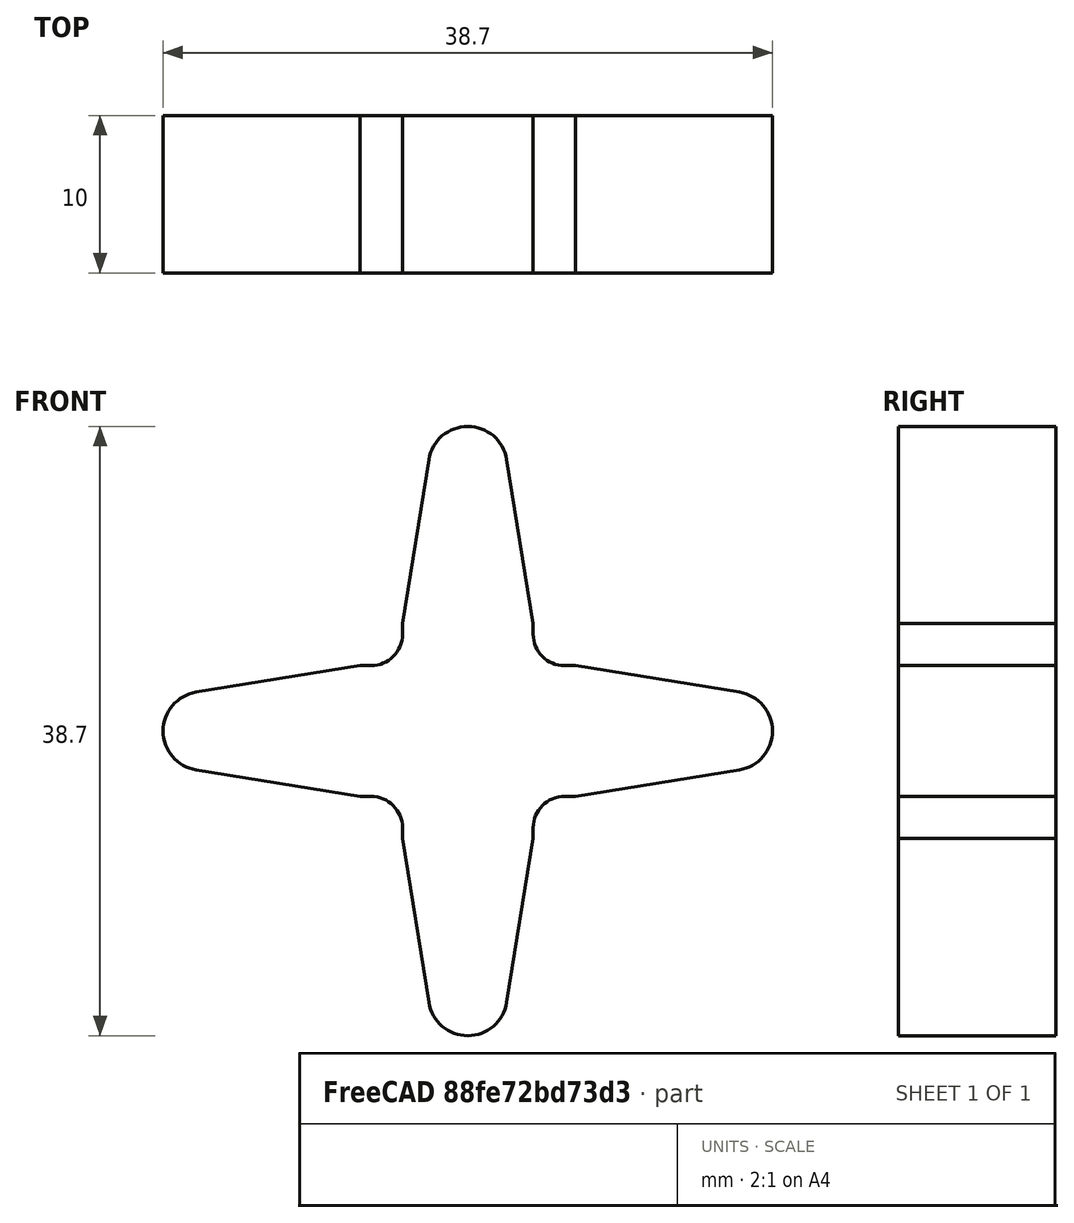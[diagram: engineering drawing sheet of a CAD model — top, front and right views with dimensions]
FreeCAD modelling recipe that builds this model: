
FCSTD DOCUMENT  (FreeCAD 0.16R6707 (Git))
Label: Corona_Futaba_3003
License: CreativeCommons Attribution-ShareAlike
LicenseURL: http://creativecommons.org/licenses/by-sa/4.0/
objects: Sketcher::SketchObject×1, PartDesign::Pad×1
note: 3 computed .brp shape members not serialized (recipe doc carries the construction recipe); baked Part::Feature solids carry a one-line shape summary decoded from their .brp

FEATURE [Sketcher::SketchObject] Sketch  label="BCT_Corona"
  Placement = pos=(0,0,0) rot=(-1,0,0;4.71239rad)
  sketch-geometry (30):
    g0: LineSegment StartX=-6.83677 StartY=4.15 StartZ=0 EndX=-6.15 EndY=4.15 EndZ=0
    g1: LineSegment StartX=-4.15 StartY=6.15 StartZ=0 EndX=-4.15 EndY=6.83677 EndZ=0
    g2: LineSegment StartX=-4.15 StartY=6.83677 StartZ=0 EndX=-2.468 EndY=17.2487 EndZ=0
    g3: LineSegment StartX=2.468 StartY=17.2487 StartZ=0 EndX=4.15 EndY=6.83677 EndZ=0
    g4: LineSegment StartX=4.15 StartY=6.83677 StartZ=0 EndX=4.15 EndY=6.15 EndZ=0
    g5: LineSegment StartX=6.15 StartY=4.15 StartZ=0 EndX=6.83677 EndY=4.15 EndZ=0
    g6: LineSegment StartX=6.83677 StartY=4.15 StartZ=0 EndX=17.2487 EndY=2.468 EndZ=0
    g7: LineSegment StartX=17.2487 StartY=-2.468 StartZ=0 EndX=6.83677 EndY=-4.15 EndZ=0
    g8: LineSegment StartX=6.83677 StartY=-4.15 StartZ=0 EndX=6.15 EndY=-4.15 EndZ=0
    g9: LineSegment StartX=4.15 StartY=-6.15 StartZ=0 EndX=4.15 EndY=-6.83677 EndZ=0
    g10: LineSegment StartX=4.15 StartY=-6.83677 StartZ=0 EndX=2.468 EndY=-17.2487 EndZ=0
    g11: LineSegment StartX=-2.468 StartY=-17.2487 StartZ=0 EndX=-4.15 EndY=-6.83677 EndZ=0
    g12: LineSegment StartX=-4.15 StartY=-6.83677 StartZ=0 EndX=-4.15 EndY=-6.15 EndZ=0
    g13: LineSegment StartX=-6.15 StartY=-4.15 StartZ=0 EndX=-6.83677 EndY=-4.15 EndZ=0
    g14: LineSegment StartX=-6.83677 StartY=-4.15 StartZ=0 EndX=-17.2487 EndY=-2.468 EndZ=0
    g15: LineSegment StartX=-17.2487 StartY=2.468 StartZ=0 EndX=-6.83677 EndY=4.15 EndZ=0
    g16: LineSegment [constr] StartX=-6.83677 StartY=4.15 StartZ=0 EndX=-6.83677 EndY=-4.15 EndZ=0
    g17: LineSegment [constr] StartX=4.15 StartY=6.83677 StartZ=0 EndX=-4.15 EndY=6.83677 EndZ=0
    g18: LineSegment [constr] StartX=6.83677 StartY=4.15 StartZ=0 EndX=6.83677 EndY=-4.15 EndZ=0
    g19: LineSegment [constr] StartX=-4.15 StartY=-6.83677 StartZ=0 EndX=4.15 EndY=-6.83677 EndZ=0
    g20: ArcOfCircle CenterX=-1e-11 CenterY=16.85 CenterZ=0 NormalX=0 NormalY=0 NormalZ=1 Radius=2.5 StartAngle=0.160161 EndAngle=2.98143
    g21: ArcOfCircle CenterX=-16.85 CenterY=-1e-12 CenterZ=0 NormalX=0 NormalY=0 NormalZ=1 Radius=2.5 StartAngle=1.73096 EndAngle=4.55223
    g22: ArcOfCircle CenterX=0 CenterY=-16.85 CenterZ=0 NormalX=0 NormalY=0 NormalZ=1 Radius=2.5 StartAngle=3.30175 EndAngle=6.12302
    g23: ArcOfCircle CenterX=16.85 CenterY=-1e-12 CenterZ=0 NormalX=0 NormalY=0 NormalZ=1 Radius=2.5 StartAngle=4.87255 EndAngle=7.69382
    g24: ArcOfCircle CenterX=6.15 CenterY=6.15 CenterZ=0 NormalX=0 NormalY=0 NormalZ=1 Radius=2 StartAngle=3.14159 EndAngle=4.71239
    g25: ArcOfCircle CenterX=6.15 CenterY=-6.15 CenterZ=0 NormalX=0 NormalY=0 NormalZ=1 Radius=2 StartAngle=1.5708 EndAngle=3.14159
    g26: ArcOfCircle CenterX=-6.15 CenterY=-6.15 CenterZ=0 NormalX=0 NormalY=0 NormalZ=1 Radius=2 StartAngle=0 EndAngle=1.5708
    g27: ArcOfCircle CenterX=-6.15 CenterY=6.15 CenterZ=0 NormalX=0 NormalY=0 NormalZ=1 Radius=2 StartAngle=4.71239 EndAngle=6.28319
    g28: LineSegment [constr] StartX=-1.1e-11 StartY=19.35 StartZ=0 EndX=0 EndY=-19.35 EndZ=0
    g29: LineSegment [constr] StartX=-19.35 StartY=0 StartZ=0 EndX=19.35 EndY=0 EndZ=0
  constraints (75):
    c: Coincident(g1,g2)
    c: Coincident(g3,g4)
    c: Vertical(g4)
    c: Coincident(g5,g6)
    c: Coincident(g7,g8)
    c: Horizontal(g8)
    c: Vertical(g9)
    c: Coincident(g9,g10)
    c: Coincident(g11,g12)
    c: Vertical(g12)
    c: Horizontal(g13)
    c: Coincident(g13,g14)
    c: Coincident(g15,g0)
    c: Equal(g0,g1)
    c: Equal(g1,g4)
    c: Equal(g4,g5)
    c: Equal(g5,g8)
    c: Equal(g8,g9)
    c: Equal(g9,g12)
    c: Equal(g12,g13)
    c: Horizontal(g5)
    c: Coincident(g16,g0)
    c: Coincident(g16,g13)
    c: Vertical(g16)
    c: Coincident(g17,g3)
    c: Coincident(g17,g1)
    c: Horizontal(g17)
    c: Equal(g16,g17)
    c: DistanceY(g16,g16) = 8.3
    c: Coincident(g18,g5)
    c: Vertical(g18)
    c: Coincident(g19,g11)
    c: Coincident(g19,g9)
    c: Horizontal(g19)
    c: Equal(g19,g18)
    c: Equal(g16,g19)
    c: Symmetric(g7,g13,g-2)
    c: Symmetric(g9,g3,g-1)
    c: Tangent(g2,g20) = 1.5708
    c: Tangent(g3,g20) = 1.5708
    c: Tangent(g14,g21) = 1.5708
    c: Tangent(g15,g21) = 1.5708
    c: Tangent(g11,g22) = 1.5708
    c: Tangent(g10,g22) = 1.5708
    c: Tangent(g6,g23) = 1.5708
    c: Tangent(g7,g23) = 1.5708
    c: Tangent(g4,g24) = -1.5708
    c: Tangent(g5,g24) = -1.5708
    c: Tangent(g9,g25) = -1.5708
    c: Tangent(g8,g25) = -1.5708
    c: Tangent(g13,g26) = -1.5708
    c: Tangent(g12,g26) = -1.5708
    c: Tangent(g0,g27) = -1.5708
    c: Tangent(g1,g27) = -1.5708
    c: Equal(g27,g24)
    c: Equal(g24,g25)
    c: Radius(g27) = 2
    c: Equal(g22,g23)
    c: Equal(g23,g20)
    c: Equal(g20,g21)
    c: Radius(g20) = 2.5
    c: Symmetric(g21,g23,g-2)
    c: PointOnObject(g28,g20)
    c: PointOnObject(g28,g22)
    c: Symmetric(g28,g28,g-1)
    c: DistanceY(g28,g28) = 38.7
    c: Symmetric(g11,g10,g-2)
    c: PointOnObject(g28,g-2)
    c: Symmetric(g3,g2,g28)
    c: PointOnObject(g29,g23)
    c: PointOnObject(g29,g21)
    c: PointOnObject(g29,g-1)
    c: PointOnObject(g29,g-1)
    c: Symmetric(g6,g7,g-1)
    c: Symmetric(g14,g15,g29)
FEATURE [PartDesign::Pad] Pad  label="Corona_Futaba_3003"
  Length = 10
  Length2 = 100
  Placement = pos=(0,0,0) rot=(-1,0,0;4.71239rad)
  Sketch = -> Sketch
  Type = 0
